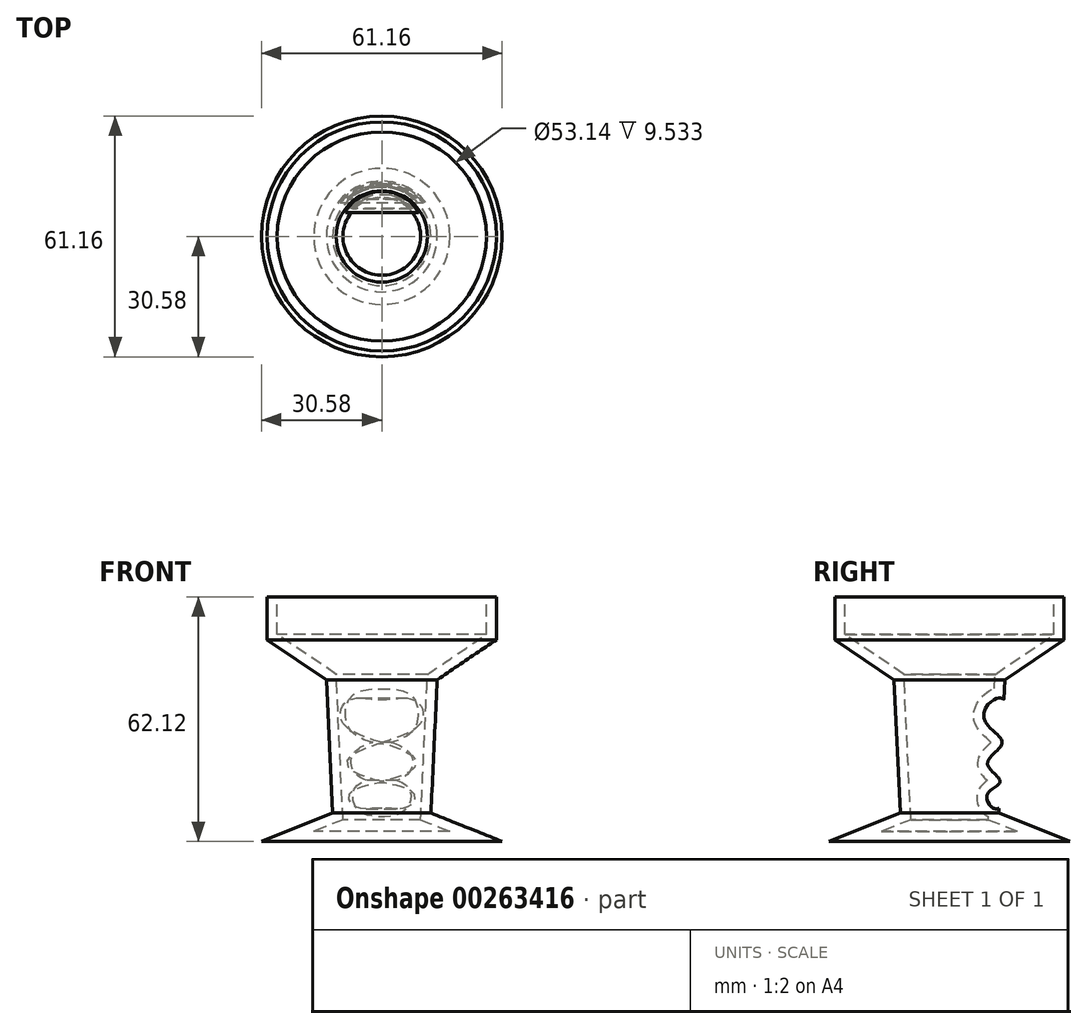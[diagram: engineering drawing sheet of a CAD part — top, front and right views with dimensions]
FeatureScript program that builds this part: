
annotation { "Feature Type Name" : "Feature", "Feature Type Description" : "" }
export const myFeature = defineFeature(function(context is Context, id is Id, definition is map)
    precondition{}
    {
        {
            var Q0;
            Q0=qCreatedBy(makeId("Front.planeOp"),FACE);
            var sketch = newSketch(context, id + "F0", { "sketchPlane" : qUnion([Q0])});
            skLineSegment(sketch, "E0", {"start": v(0, 0) * mm, "end": v(-30.58, 0) * mm});
            skLineSegment(sketch, "E1", {"start": v(-30.58, 0) * mm, "end": v(-12.48, 7.18) * mm});
            skLineSegment(sketch, "E2", {"start": v(-12.48, 7.18) * mm, "end": v(-14.08, 41.06) * mm});
            skLineSegment(sketch, "E3", {"start": v(0, 37.35) * mm, "end": v(0, 0) * mm});
            skLineSegment(sketch, "E4", {"start": v(-14.08, 41.06) * mm, "end": v(-29.1, 51.24) * mm});
            skLineSegment(sketch, "E5", {"start": v(-29.1, 51.24) * mm, "end": v(-29.1, 62.12) * mm});
            skLineSegment(sketch, "E6", {"start": v(-29.1, 62.12) * mm, "end": v(0, 62.12) * mm});
            skLineSegment(sketch, "E7", {"start": v(0, 62.12) * mm, "end": v(0, 37.35) * mm});
            skSolve(sketch);
        }
        {
            var Q0;
            Q0=makeQuery(id+"F0.imprint","IMPRINT",FACE,{"disambiguationData":[TD([[makeQuery(id+"F0.imprint","IMPRINT",EDGE,{"derivedFrom":sQuery(id+"F0.wireOp",EDGE,"E0")}),-1.0]])]});
            var Q1;
            Q1=sQuery(id+"F0.wireOp",EDGE,"E7");
            revolve(context, id + "F1", {"entities" : qUnion([Q0]), "axis" : qUnion([Q1]), "revolveType" : RevolveType.FULL});
        }
        {
            var Q0;
            Q0=qCreatedBy(makeId("Right.planeOp"),FACE);
            var sketch = newSketch(context, id + "F2", { "sketchPlane" : qUnion([Q0])});
            skLineSegment(sketch, "E8", {"start": v(14.08, 41.06) * mm, "end": v(12.48, 7.18) * mm});
            skFitSpline(sketch, "E9", {"points": [v(13.84, 36.08) * mm, v(8.66, 31.7) * mm, v(13.33, 25.15) * mm, v(9.63, 19.83) * mm, v(12.86, 15.19) * mm, v(9.5, 11.6) * mm, v(12.54, 8.44) * mm, v(13.84, 36.08) * mm]});
            skSolve(sketch);
        }
        {
            var Q0;
            Q0 = qSketchRegion(id + "F2", true);
            extrude(context, id + "F3", {"entities" : qUnion([Q0]), "operationType" : NewBodyOperationType.REMOVE, "endBound" : BoundingType.SYMMETRIC, "depth" : 254 * mm});
        }
        {
            var Q0;
            Q0=makeQuery(id+"F1.opRevolve","SWEPT_FACE",FACE,{"disambiguationData":[OSD([sQuery(id+"F0.wireOp",EDGE,"E6")])]});
            shell(context, id + "F4", {"entities" : qUnion([Q0]), "thickness" : 2.54 * mm});
        }
    });
